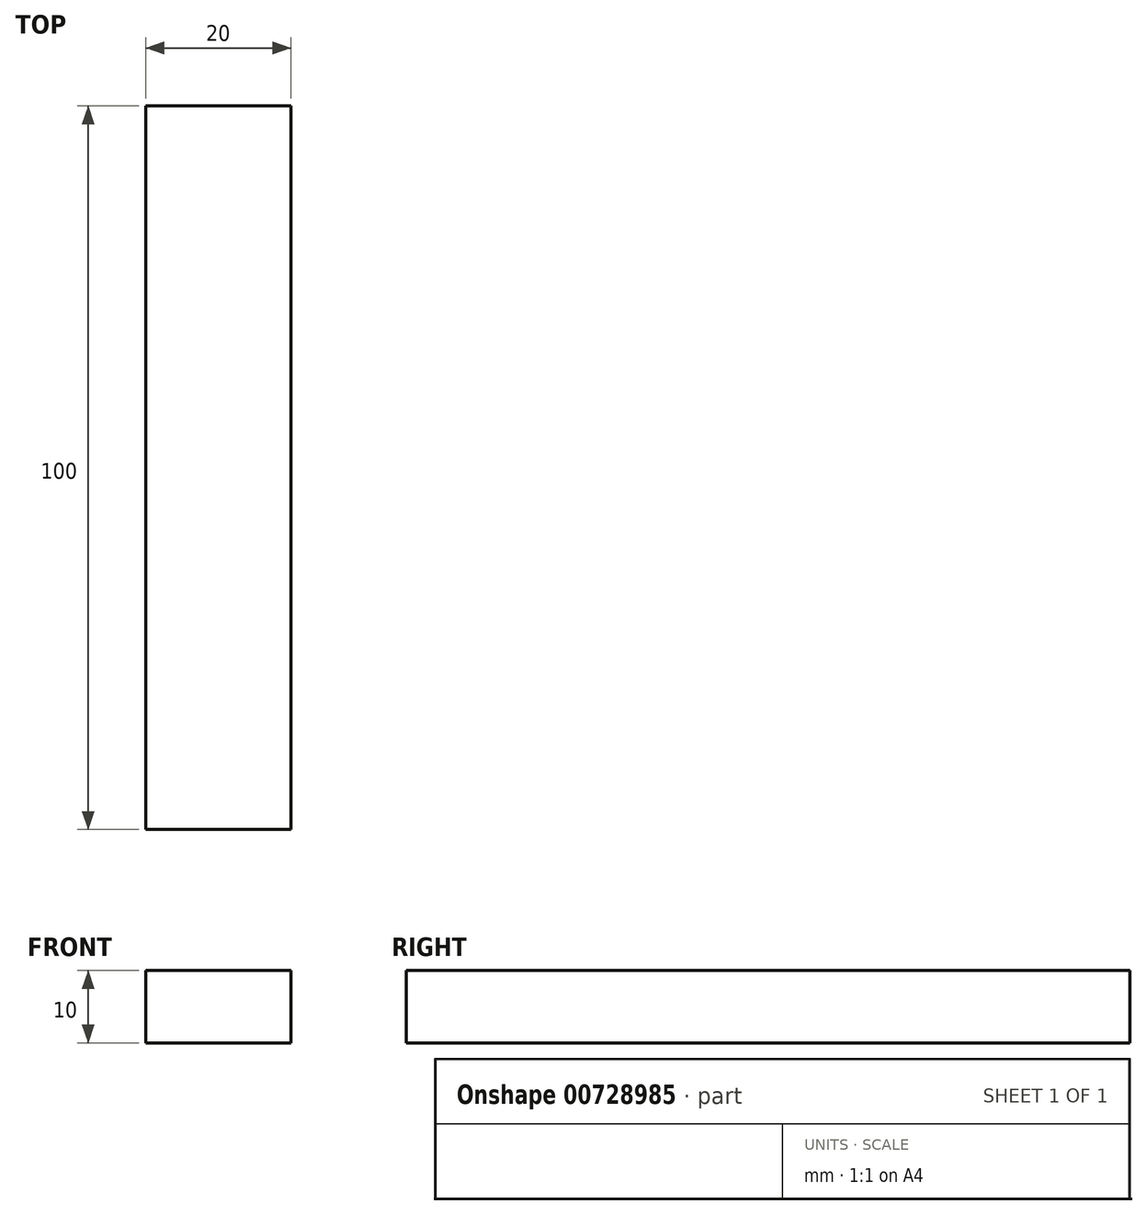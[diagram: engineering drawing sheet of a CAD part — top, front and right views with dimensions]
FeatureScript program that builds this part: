
annotation { "Feature Type Name" : "Feature", "Feature Type Description" : "" }
export const myFeature = defineFeature(function(context is Context, id is Id, definition is map)
    precondition{}
    {
        {
            var Q0;
            Q0=qCreatedBy(makeId("Right.planeOp"),FACE);
            var sketch = newSketch(context, id + "F0", { "sketchPlane" : qUnion([Q0])});
            skLineSegment(sketch, "E0.bottom", {"start": v(50, 5) * mm, "end": v(-50, 5) * mm});
            skLineSegment(sketch, "E0.top", {"start": v(50, -5) * mm, "end": v(-50, -5) * mm});
            skLineSegment(sketch, "E0.left", {"start": v(50, 5) * mm, "end": v(50, -5) * mm});
            skLineSegment(sketch, "E0.right", {"start": v(-50, 5) * mm, "end": v(-50, -5) * mm});
            skPoint(sketch, "E0.middle", {"position": v(0, 0) * mm});
            skSolve(sketch);
        }
        {
            var Q0;
            Q0=makeQuery(id+"F0.imprint","IMPRINT",FACE,{"disambiguationData":[TD([[makeQuery(id+"F0.imprint","IMPRINT",EDGE,{"derivedFrom":sQuery(id+"F0.wireOp",EDGE,"E0.bottom")}),1.0]])]});
            extrude(context, id + "F1", {"entities" : qUnion([Q0]), "depth" : 20 * mm, "offsetDistance" : 25 * mm});
        }
    });
